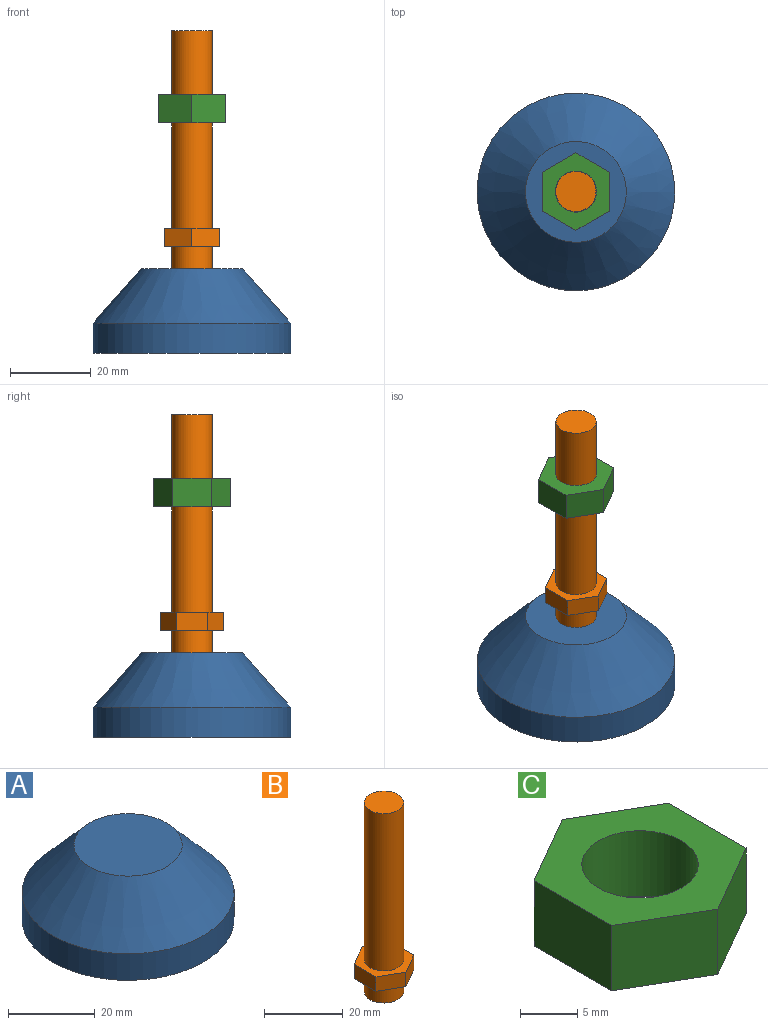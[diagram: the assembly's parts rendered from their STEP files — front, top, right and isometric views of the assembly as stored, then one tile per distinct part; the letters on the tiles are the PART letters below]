
ASSEMBLY  parts=3 mates=2
PART A: 4 faces, bbox 49x49x21 mm
  f0: plane 49x49mm, normal (0,0,-1), area 1885.7mm2, adj f1
  f1: cylinder r=24.5mm len=49mm, axis (0,0,1), area 1154.5mm2, adj f0,f2
  f2: cone r=24.5mm half-angle=41.6deg, axis (0,0,-1), area 2099.6mm2, adj f1,f3
  f3: plane 25x25mm, normal (0,0,1), area 490.9mm2, adj f2
PART B: 12 faces, bbox 13.7x15.8x59 mm
  f0: cylinder r=5mm len=10mm, axis (0,0,-1), area 172.8mm2, adj f1,f8
  f1: plane 10x10mm, normal (0,0,-1), area 78.5mm2, adj f0
  f2: plane 6.83x4.5mm, normal (-0.5,-0.87,0), area 35.5mm2, adj f3,f7,f8,f9
  f3: plane 6.83x4.5mm, normal (0.5,-0.87,0), area 35.5mm2, adj f2,f4,f8,f9
  f4: plane 7.88x4.5mm, normal (1,0,0), area 35.5mm2, adj f3,f5,f8,f9
  f5: plane 6.83x4.5mm, normal (0.5,0.87,0), area 35.5mm2, adj f4,f6,f8,f9
  f6: plane 6.83x4.5mm, normal (-0.5,0.87,0), area 35.5mm2, adj f5,f7,f8,f9
  f7: plane 7.88x4.5mm, normal (-1,0,0), area 35.5mm2, adj f2,f6,f8,f9
  f8: plane 15.76x13.65mm, normal (0,0,-1), area 82.8mm2, adj f0,f2,f3,f4,f5,f6,f7
  f9: plane 15.76x13.65mm, normal (0,0,1), area 82.8mm2, adj f2,f3,f4,f5,f6,f7,f10
  f10: cylinder r=5mm len=49mm, axis (0,0,-1), area 1539.4mm2, adj f9,f11
  f11: plane 10x10mm, normal (0,0,1), area 78.5mm2, adj f10
PART C: 9 faces, bbox 16.7x19.2x7 mm
  f0: plane 8.33x7mm, normal (-0.5,-0.87,0), area 67.3mm2, adj f1,f6,f7,f8
  f1: plane 8.33x7mm, normal (0.5,-0.87,0), area 67.3mm2, adj f0,f2,f7,f8
  f2: plane 9.61x7mm, normal (1,0,0), area 67.3mm2, adj f1,f3,f7,f8
  f3: plane 8.33x7mm, normal (0.5,0.87,0), area 67.3mm2, adj f2,f4,f7,f8
  f4: plane 8.33x7mm, normal (-0.5,0.87,0), area 67.3mm2, adj f3,f6,f7,f8
  f5: cylinder r=5.1mm len=10.2mm, axis (0,0,1), area 224.3mm2, adj f7,f8
  f6: plane 9.61x7mm, normal (-1,0,0), area 67.3mm2, adj f0,f4,f7,f8
  f7: plane 19.23x16.65mm, normal (0,0,-1), area 158.4mm2, adj f0,f1,f2,f3,f4,f5,f6
  f8: plane 19.23x16.65mm, normal (0,0,1), area 158.4mm2, adj f0,f1,f2,f3,f4,f5,f6
PLACE A at identity fixed
PLACE B at identity
PLACE C t=(0,0,-15.81)mm
MATE fastened B.f0 <-> A.f1  axis (0,0,-1) through (0,0,21)mm
MATE slider B.f0 <-> C.f5  axis (0,0,-1) through (0,0,80)mm
